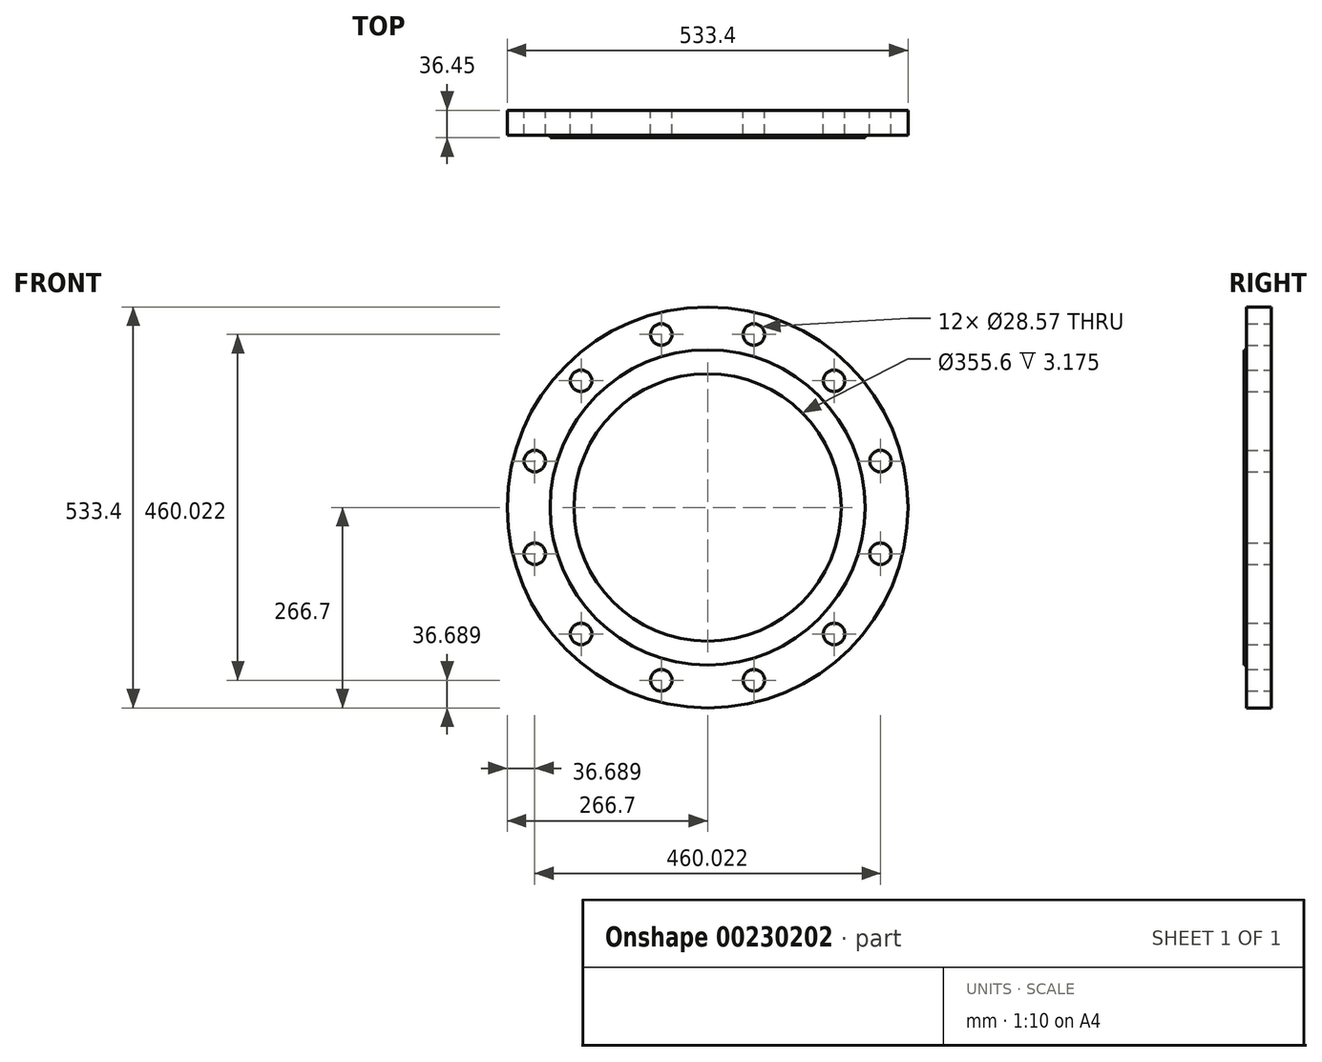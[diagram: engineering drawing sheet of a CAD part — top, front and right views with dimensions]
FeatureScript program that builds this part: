
annotation { "Feature Type Name" : "Feature", "Feature Type Description" : "" }
export const myFeature = defineFeature(function(context is Context, id is Id, definition is map)
    precondition{}
    {
        {
            var Q0;
            Q0=qCreatedBy(makeId("Front.planeOp"),FACE);
            var sketch = newSketch(context, id + "F0", { "sketchPlane" : qUnion([Q0])});
            skCircle(sketch, "E0", {"center": v(0, 0) * mm, "radius": 177.8 * mm});
            skCircle(sketch, "E1", {"center": v(0, 0) * mm, "radius": 266.7 * mm});
            skCircle(sketch, "E2", {"center": v(61.63, 230.01) * mm, "radius": 14.29 * mm});
            skCircle(sketch, "E3.1.0", {"center": v(-61.63, 230.01) * mm, "radius": 14.29 * mm});
            skCircle(sketch, "E3.2.0", {"center": v(-168.38, 168.38) * mm, "radius": 14.29 * mm});
            skCircle(sketch, "E3.3.0", {"center": v(-230.01, 61.63) * mm, "radius": 14.29 * mm});
            skCircle(sketch, "E3.4.0", {"center": v(-230.01, -61.63) * mm, "radius": 14.29 * mm});
            skCircle(sketch, "E3.5.0", {"center": v(-168.38, -168.38) * mm, "radius": 14.29 * mm});
            skCircle(sketch, "E3.6.0", {"center": v(-61.63, -230.01) * mm, "radius": 14.29 * mm});
            skCircle(sketch, "E3.7.0", {"center": v(61.63, -230.01) * mm, "radius": 14.29 * mm});
            skCircle(sketch, "E3.8.0", {"center": v(168.38, -168.38) * mm, "radius": 14.29 * mm});
            skCircle(sketch, "E3.9.0", {"center": v(230.01, -61.63) * mm, "radius": 14.29 * mm});
            skCircle(sketch, "E3.10.0", {"center": v(230.01, 61.63) * mm, "radius": 14.29 * mm});
            skCircle(sketch, "E3.11.0", {"center": v(168.38, 168.38) * mm, "radius": 14.29 * mm});
            skSolve(sketch);
        }
        {
            var Q0;
            Q0 = qSketchRegion(id + "F0", true);
            extrude(context, id + "F1", {"entities" : qUnion([Q0]), "depth" : 33.27 * mm});
        }
        {
            var Q0;
            Q0=makeQuery(id+"F1.opExtrude","CAP_FACE",FACE,{"disambiguationData":[OSD([sQuery(id+"F0.wireOp",EDGE,"E0"),sQuery(id+"F0.wireOp",EDGE,"E1"),sQuery(id+"F0.wireOp",EDGE,"E2"),sQuery(id+"F0.wireOp",EDGE,"E3.1.0"),sQuery(id+"F0.wireOp",EDGE,"E3.2.0"),sQuery(id+"F0.wireOp",EDGE,"E3.3.0"),sQuery(id+"F0.wireOp",EDGE,"E3.4.0"),sQuery(id+"F0.wireOp",EDGE,"E3.5.0"),sQuery(id+"F0.wireOp",EDGE,"E3.6.0"),sQuery(id+"F0.wireOp",EDGE,"E3.7.0"),sQuery(id+"F0.wireOp",EDGE,"E3.8.0"),sQuery(id+"F0.wireOp",EDGE,"E3.9.0"),sQuery(id+"F0.wireOp",EDGE,"E3.10.0"),sQuery(id+"F0.wireOp",EDGE,"E3.11.0")])],"isStart":false});
            var sketch = newSketch(context, id + "F2", { "sketchPlane" : qUnion([Q0])});
            skCircle(sketch, "E4", {"center": v(0, 0) * mm, "radius": 209.55 * mm});
            skCircle(sketch, "E5", {"center": v(0, 0) * mm, "radius": 177.8 * mm});
            skSolve(sketch);
        }
        {
            var Q0;
            Q0 = qSketchRegion(id + "F2", true);
            extrude(context, id + "F3", {"entities" : qUnion([Q0]), "operationType" : NewBodyOperationType.ADD, "depth" : 3.17 * mm});
        }
        {
            var Q0;
            Q0=makeQuery(id+"F1.opExtrude","CAP_FACE",FACE,{"disambiguationData":[OSD([sQuery(id+"F0.wireOp",EDGE,"E0"),sQuery(id+"F0.wireOp",EDGE,"E1"),sQuery(id+"F0.wireOp",EDGE,"E2"),sQuery(id+"F0.wireOp",EDGE,"E3.1.0"),sQuery(id+"F0.wireOp",EDGE,"E3.2.0"),sQuery(id+"F0.wireOp",EDGE,"E3.3.0"),sQuery(id+"F0.wireOp",EDGE,"E3.4.0"),sQuery(id+"F0.wireOp",EDGE,"E3.5.0"),sQuery(id+"F0.wireOp",EDGE,"E3.6.0"),sQuery(id+"F0.wireOp",EDGE,"E3.7.0"),sQuery(id+"F0.wireOp",EDGE,"E3.8.0"),sQuery(id+"F0.wireOp",EDGE,"E3.9.0"),sQuery(id+"F0.wireOp",EDGE,"E3.10.0"),sQuery(id+"F0.wireOp",EDGE,"E3.11.0")])],"isStart":false});
            var sketch = newSketch(context, id + "F4", { "sketchPlane" : qUnion([Q0])});
            skCircle(sketch, "E6", {"center": v(0, 0) * mm, "radius": 177.8 * mm});
            skSolve(sketch);
        }
        {
            var Q0;
            Q0 = qSketchRegion(id + "F4", true);
            extrude(context, id + "F5", {"entities" : qUnion([Q0]), "operationType" : NewBodyOperationType.ADD, "oppositeDirection" : true, "depth" : 33.27 * mm});
        }
    });
